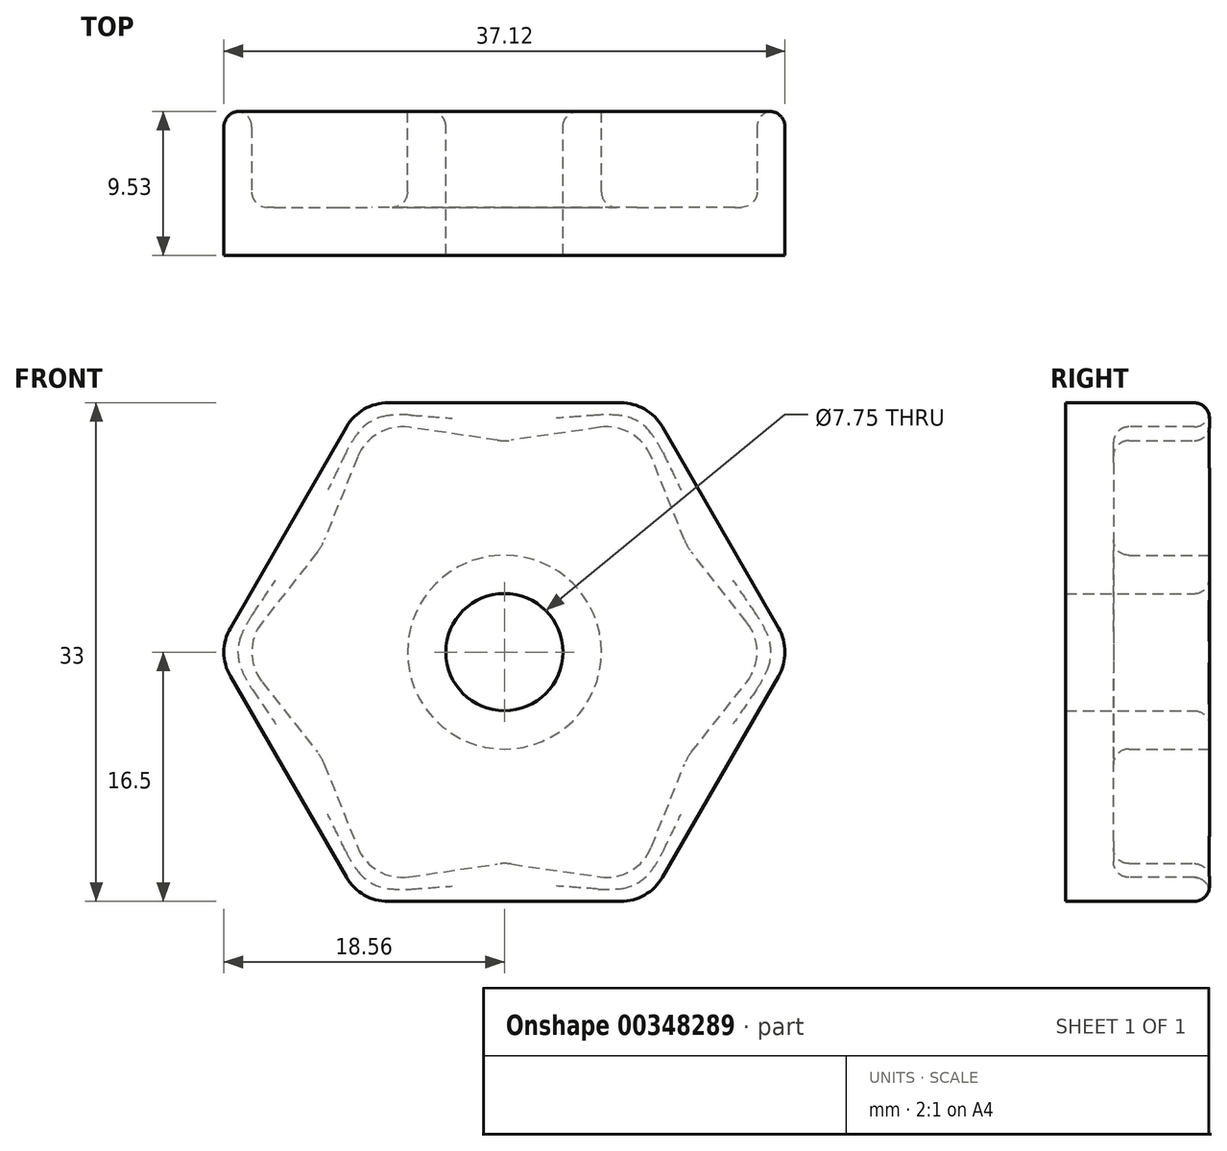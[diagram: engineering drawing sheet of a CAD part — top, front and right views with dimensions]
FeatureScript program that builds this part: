
annotation { "Feature Type Name" : "Feature", "Feature Type Description" : "" }
export const myFeature = defineFeature(function(context is Context, id is Id, definition is map)
    precondition{}
    {
        {
            var Q0;
            Q0=qCreatedBy(makeId("Front.planeOp"),FACE);
            var sketch = newSketch(context, id + "F0", { "sketchPlane" : qUnion([Q0])});
            skCircle(sketch, "E0.cCircle", {"center": v(0, 0) * mm, "radius": 16.5 * mm, "construction": true});
            skLineSegment(sketch, "E0.0", {"start": v(9.53, 16.5) * mm, "end": v(19.05, 0) * mm});
            skLineSegment(sketch, "E0.1", {"start": v(19.05, 0) * mm, "end": v(9.53, -16.5) * mm});
            skLineSegment(sketch, "E0.2", {"start": v(9.52, -16.5) * mm, "end": v(-9.53, -16.5) * mm});
            skLineSegment(sketch, "E0.3", {"start": v(-9.53, -16.5) * mm, "end": v(-19.05, 0) * mm});
            skLineSegment(sketch, "E0.4", {"start": v(-19.05, 0) * mm, "end": v(-9.52, 16.5) * mm});
            skLineSegment(sketch, "E0.5", {"start": v(-9.52, 16.5) * mm, "end": v(9.53, 16.5) * mm});
            skPoint(sketch, "E0.0.midPoint", {"position": v(14.29, 8.25) * mm});
            skLineSegment(sketch, "E1", {"start": v(0, 0) * mm, "end": v(-19.05, 0) * mm, "construction": true});
            skCircle(sketch, "E2", {"center": v(0, 0) * mm, "radius": 3.87 * mm});
            skSolve(sketch);
        }
        {
            var Q0;
            Q0 = qSketchRegion(id + "F0", true);
            extrude(context, id + "F1", {"entities" : qUnion([Q0]), "depth" : 9.52 * mm});
        }
        {
            var Q0;
            Q0=makeQuery(id+"F1.opExtrude","CAP_FACE",FACE,{"disambiguationData":[OSD([sQuery(id+"F0.wireOp",EDGE,"E0.0"),sQuery(id+"F0.wireOp",EDGE,"E0.1"),sQuery(id+"F0.wireOp",EDGE,"E0.2"),sQuery(id+"F0.wireOp",EDGE,"E0.3"),sQuery(id+"F0.wireOp",EDGE,"E0.4"),sQuery(id+"F0.wireOp",EDGE,"E0.5"),sQuery(id+"F0.wireOp",EDGE,"E2")])],"isStart":true});
            var sketch = newSketch(context, id + "F2", { "sketchPlane" : qUnion([Q0])});
            skLineSegment(sketch, "E3.0", {"start": v(-8.8, 15.23) * mm, "end": v(-17.58, 0) * mm, "construction": true});
            skLineSegment(sketch, "E3.1", {"start": v(-8.8, -15.23) * mm, "end": v(8.8, -15.23) * mm, "construction": true});
            skLineSegment(sketch, "E3.2", {"start": v(8.8, -15.23) * mm, "end": v(17.58, 0) * mm, "construction": true});
            skLineSegment(sketch, "E3.3", {"start": v(-17.58, 0) * mm, "end": v(-8.8, -15.23) * mm, "construction": true});
            skLineSegment(sketch, "E3.4", {"start": v(17.58, 0) * mm, "end": v(8.8, 15.23) * mm, "construction": true});
            skLineSegment(sketch, "E3.5", {"start": v(8.8, 15.23) * mm, "end": v(-8.8, 15.23) * mm, "construction": true});
            skCircle(sketch, "E4.0", {"center": v(0, 0) * mm, "radius": 6.41 * mm});
            skLineSegment(sketch, "E5", {"start": v(-17.58, 0) * mm, "end": v(-12.09, 6.98) * mm});
            skLineSegment(sketch, "E6", {"start": v(-12.09, 6.98) * mm, "end": v(-8.8, 15.23) * mm});
            skLineSegment(sketch, "E7", {"start": v(0, 0) * mm, "end": v(-13.19, 7.61) * mm, "construction": true});
            skLineSegment(sketch, "E8.1.0", {"start": v(-8.8, -15.23) * mm, "end": v(-12.09, -6.98) * mm});
            skLineSegment(sketch, "E8.1.1", {"start": v(-12.09, -6.98) * mm, "end": v(-17.58, 0) * mm});
            skLineSegment(sketch, "E8.2.0", {"start": v(8.8, -15.23) * mm, "end": v(0, -13.96) * mm});
            skLineSegment(sketch, "E8.2.1", {"start": v(0, -13.96) * mm, "end": v(-8.8, -15.23) * mm});
            skLineSegment(sketch, "E8.3.0", {"start": v(17.58, 0) * mm, "end": v(12.09, -6.98) * mm});
            skLineSegment(sketch, "E8.3.1", {"start": v(12.09, -6.98) * mm, "end": v(8.8, -15.23) * mm});
            skLineSegment(sketch, "E8.4.0", {"start": v(8.8, 15.23) * mm, "end": v(12.09, 6.98) * mm});
            skLineSegment(sketch, "E8.4.1", {"start": v(12.09, 6.98) * mm, "end": v(17.58, 0) * mm});
            skLineSegment(sketch, "E8.5.0", {"start": v(-8.8, 15.23) * mm, "end": v(0, 13.96) * mm});
            skLineSegment(sketch, "E8.5.1", {"start": v(0, 13.96) * mm, "end": v(8.8, 15.23) * mm});
            skSolve(sketch);
        }
        {
            var Q0;
            Q0 = qSketchRegion(id + "F2", true);
            extrude(context, id + "F3", {"entities" : qUnion([Q0]), "operationType" : NewBodyOperationType.REMOVE, "oppositeDirection" : true, "depth" : 6.35 * mm});
        }
        {
            var Q0;
            Q0=makeQuery(id+"F3.boolean.opBoolean","COPY",EDGE,{"derivedFrom":makeQuery(id+"F3.opExtrude","SWEPT_EDGE",EDGE,{"disambiguationData":[OSD([sQuery(id+"F2.wireOp",EDGE,"E8.3.0"),sQuery(id+"F2.wireOp",EDGE,"E8.4.1")])]})});
            var Q1;
            Q1=makeQuery(id+"F3.boolean.opBoolean","COPY",EDGE,{"derivedFrom":makeQuery(id+"F3.opExtrude","SWEPT_EDGE",EDGE,{"disambiguationData":[OSD([sQuery(id+"F2.wireOp",EDGE,"E8.4.0"),sQuery(id+"F2.wireOp",EDGE,"E8.4.1")])]})});
            var Q2;
            Q2=makeQuery(id+"F3.boolean.opBoolean","COPY",EDGE,{"derivedFrom":makeQuery(id+"F3.opExtrude","SWEPT_EDGE",EDGE,{"disambiguationData":[OSD([sQuery(id+"F2.wireOp",EDGE,"E8.4.0"),sQuery(id+"F2.wireOp",EDGE,"E8.5.1")])]})});
            var Q3;
            Q3=makeQuery(id+"F3.boolean.opBoolean","COPY",EDGE,{"derivedFrom":makeQuery(id+"F3.opExtrude","SWEPT_EDGE",EDGE,{"disambiguationData":[OSD([sQuery(id+"F2.wireOp",EDGE,"E8.5.0"),sQuery(id+"F2.wireOp",EDGE,"E8.5.1")])]})});
            var Q4;
            Q4=makeQuery(id+"F3.boolean.opBoolean","COPY",EDGE,{"derivedFrom":makeQuery(id+"F3.opExtrude","SWEPT_EDGE",EDGE,{"disambiguationData":[OSD([sQuery(id+"F2.wireOp",EDGE,"E6"),sQuery(id+"F2.wireOp",EDGE,"E8.5.0")])]})});
            var Q5;
            Q5=makeQuery(id+"F3.boolean.opBoolean","COPY",EDGE,{"derivedFrom":makeQuery(id+"F3.opExtrude","SWEPT_EDGE",EDGE,{"disambiguationData":[OSD([sQuery(id+"F2.wireOp",EDGE,"E5"),sQuery(id+"F2.wireOp",EDGE,"E6")])]})});
            var Q6;
            Q6=makeQuery(id+"F3.boolean.opBoolean","COPY",EDGE,{"derivedFrom":makeQuery(id+"F3.opExtrude","SWEPT_EDGE",EDGE,{"disambiguationData":[OSD([sQuery(id+"F2.wireOp",EDGE,"E5"),sQuery(id+"F2.wireOp",EDGE,"E8.1.1")])]})});
            var Q7;
            Q7=makeQuery(id+"F3.boolean.opBoolean","COPY",EDGE,{"derivedFrom":makeQuery(id+"F3.opExtrude","SWEPT_EDGE",EDGE,{"disambiguationData":[OSD([sQuery(id+"F2.wireOp",EDGE,"E8.1.0"),sQuery(id+"F2.wireOp",EDGE,"E8.1.1")])]})});
            var Q8;
            Q8=makeQuery(id+"F3.boolean.opBoolean","COPY",EDGE,{"derivedFrom":makeQuery(id+"F3.opExtrude","SWEPT_EDGE",EDGE,{"disambiguationData":[OSD([sQuery(id+"F2.wireOp",EDGE,"E8.1.0"),sQuery(id+"F2.wireOp",EDGE,"E8.2.1")])]})});
            var Q9;
            Q9=makeQuery(id+"F3.boolean.opBoolean","COPY",EDGE,{"derivedFrom":makeQuery(id+"F3.opExtrude","SWEPT_EDGE",EDGE,{"disambiguationData":[OSD([sQuery(id+"F2.wireOp",EDGE,"E8.2.0"),sQuery(id+"F2.wireOp",EDGE,"E8.2.1")])]})});
            var Q10;
            Q10=makeQuery(id+"F3.boolean.opBoolean","COPY",EDGE,{"derivedFrom":makeQuery(id+"F3.opExtrude","SWEPT_EDGE",EDGE,{"disambiguationData":[OSD([sQuery(id+"F2.wireOp",EDGE,"E8.2.0"),sQuery(id+"F2.wireOp",EDGE,"E8.3.1")])]})});
            var Q11;
            Q11=makeQuery(id+"F3.boolean.opBoolean","COPY",EDGE,{"derivedFrom":makeQuery(id+"F3.opExtrude","SWEPT_EDGE",EDGE,{"disambiguationData":[OSD([sQuery(id+"F2.wireOp",EDGE,"E8.3.0"),sQuery(id+"F2.wireOp",EDGE,"E8.3.1")])]})});
            var Q12;
            Q12=makeQuery(id+"F1.opExtrude","SWEPT_EDGE",EDGE,{"disambiguationData":[OSD([sQuery(id+"F0.wireOp",EDGE,"E0.4"),sQuery(id+"F0.wireOp",EDGE,"E0.5")])]});
            var Q13;
            Q13=makeQuery(id+"F1.opExtrude","SWEPT_EDGE",EDGE,{"disambiguationData":[OSD([sQuery(id+"F0.wireOp",EDGE,"E0.0"),sQuery(id+"F0.wireOp",EDGE,"E0.5")])]});
            var Q14;
            Q14=makeQuery(id+"F1.opExtrude","SWEPT_EDGE",EDGE,{"disambiguationData":[OSD([sQuery(id+"F0.wireOp",EDGE,"E0.0"),sQuery(id+"F0.wireOp",EDGE,"E0.1")])]});
            var Q15;
            Q15=makeQuery(id+"F1.opExtrude","SWEPT_EDGE",EDGE,{"disambiguationData":[OSD([sQuery(id+"F0.wireOp",EDGE,"E0.1"),sQuery(id+"F0.wireOp",EDGE,"E0.2")])]});
            var Q16;
            Q16=makeQuery(id+"F1.opExtrude","SWEPT_EDGE",EDGE,{"disambiguationData":[OSD([sQuery(id+"F0.wireOp",EDGE,"E0.3"),sQuery(id+"F0.wireOp",EDGE,"E0.4")])]});
            var Q17;
            Q17=makeQuery(id+"F1.opExtrude","SWEPT_EDGE",EDGE,{"disambiguationData":[OSD([sQuery(id+"F0.wireOp",EDGE,"E0.2"),sQuery(id+"F0.wireOp",EDGE,"E0.3")])]});
            fillet(context, id + "F4", {"entities" : qUnion([Q0, Q1, Q2, Q3, Q4, Q5, Q6, Q7, Q8, Q9, Q10, Q11, Q12, Q13, Q14, Q15, Q16, Q17]), "radius" : 3.18 * mm, "tangentPropagation" : true, "allowEdgeOverflow" : false});
        }
        {
            var Q0;
            Q0=makeQuery(id+"F3.boolean.opBoolean","COPY",FACE,{"derivedFrom":makeQuery(id+"F3.opExtrude","CAP_FACE",FACE,{"disambiguationData":[OSD([sQuery(id+"F2.wireOp",EDGE,"E4.0"),sQuery(id+"F2.wireOp",EDGE,"E5"),sQuery(id+"F2.wireOp",EDGE,"E6"),sQuery(id+"F2.wireOp",EDGE,"E8.1.0"),sQuery(id+"F2.wireOp",EDGE,"E8.1.1"),sQuery(id+"F2.wireOp",EDGE,"E8.2.0"),sQuery(id+"F2.wireOp",EDGE,"E8.2.1"),sQuery(id+"F2.wireOp",EDGE,"E8.3.0"),sQuery(id+"F2.wireOp",EDGE,"E8.3.1"),sQuery(id+"F2.wireOp",EDGE,"E8.4.0"),sQuery(id+"F2.wireOp",EDGE,"E8.4.1"),sQuery(id+"F2.wireOp",EDGE,"E8.5.0"),sQuery(id+"F2.wireOp",EDGE,"E8.5.1")])],"isStart":false})});
            var Q1;
            Q1=makeQuery(id+"F3.boolean.opBoolean","COPY",EDGE,{"derivedFrom":makeQuery(id+"F3.opExtrude","CAP_EDGE",EDGE,{"disambiguationData":[OSD([sQuery(id+"F2.wireOp",EDGE,"E4.0")])],"isStart":true})});
            var Q2;
            Q2=makeQuery(id+"F1.opExtrude","CAP_EDGE",EDGE,{"disambiguationData":[OSD([sQuery(id+"F0.wireOp",EDGE,"E2")])],"isStart":true});
            var Q3;
            {var subQ0=sQuery(id+"F2.wireOp",EDGE,"E8.1.1");var subQ1=sQuery(id+"F0.wireOp",EDGE,"E0.5");var subQ2=sQuery(id+"F2.wireOp",EDGE,"E5");var subQ3=sQuery(id+"F0.wireOp",EDGE,"E0.4");var subQ4=sQuery(id+"F0.wireOp",EDGE,"E0.0");var subQ5=sQuery(id+"F0.wireOp",EDGE,"E0.3");var subQ6=sQuery(id+"F0.wireOp",EDGE,"E0.1");var subQ7=sQuery(id+"F0.wireOp",EDGE,"E0.2");Q3=makeQuery(id+"F4.opFillet","BLEND_EDGE",EDGE,{"blendedFrom":[makeQuery(id+"F3.boolean.opBoolean","COPY",EDGE,{"derivedFrom":makeQuery(id+"F3.opExtrude","SWEPT_EDGE",EDGE,{"disambiguationData":[OSD([subQ2,subQ0])]})}),makeQuery(id+"F3.boolean.opBoolean","SPLIT",FACE,{"disambiguationData":[TD([makeQuery(id+"F1.opExtrude","SWEPT_FACE",FACE,{"disambiguationData":[OSD([subQ4])]})])],"derivedFrom":makeQuery(id+"F1.opExtrude","CAP_FACE",FACE,{"disambiguationData":[OSD([subQ4,subQ6,subQ7,subQ5,subQ3,subQ1,sQuery(id+"F0.wireOp",EDGE,"E2")])],"isStart":true})})],"blendedInto":[makeQuery(id+"F3.boolean.opBoolean","SPLIT",FACE,{"disambiguationData":[TD([makeQuery(id+"F1.opExtrude","SWEPT_FACE",FACE,{"disambiguationData":[OSD([subQ4])]})])],"derivedFrom":makeQuery(id+"F1.opExtrude","CAP_FACE",FACE,{"disambiguationData":[OSD([subQ4,subQ6,subQ7,subQ5,subQ3,subQ1,sQuery(id+"F0.wireOp",EDGE,"E2")])],"isStart":true})})]});}
            var Q4;
            {var subQ0=sQuery(id+"F0.wireOp",EDGE,"E0.5");var subQ1=sQuery(id+"F0.wireOp",EDGE,"E0.4");var subQ2=sQuery(id+"F0.wireOp",EDGE,"E0.0");var subQ3=sQuery(id+"F0.wireOp",EDGE,"E0.3");var subQ4=sQuery(id+"F0.wireOp",EDGE,"E0.1");var subQ5=sQuery(id+"F0.wireOp",EDGE,"E0.2");Q4=makeQuery(id+"F4.opFillet","BLEND_EDGE",EDGE,{"blendedFrom":[makeQuery(id+"F1.opExtrude","SWEPT_EDGE",EDGE,{"disambiguationData":[OSD([subQ2,subQ4])]}),makeQuery(id+"F3.boolean.opBoolean","SPLIT",FACE,{"disambiguationData":[TD([makeQuery(id+"F1.opExtrude","SWEPT_FACE",FACE,{"disambiguationData":[OSD([subQ2])]})])],"derivedFrom":makeQuery(id+"F1.opExtrude","CAP_FACE",FACE,{"disambiguationData":[OSD([subQ2,subQ4,subQ5,subQ3,subQ1,subQ0,sQuery(id+"F0.wireOp",EDGE,"E2")])],"isStart":true})})],"blendedInto":[makeQuery(id+"F3.boolean.opBoolean","SPLIT",FACE,{"disambiguationData":[TD([makeQuery(id+"F1.opExtrude","SWEPT_FACE",FACE,{"disambiguationData":[OSD([subQ2])]})])],"derivedFrom":makeQuery(id+"F1.opExtrude","CAP_FACE",FACE,{"disambiguationData":[OSD([subQ2,subQ4,subQ5,subQ3,subQ1,subQ0,sQuery(id+"F0.wireOp",EDGE,"E2")])],"isStart":true})})]});}
            fillet(context, id + "F5", {"entities" : qUnion([Q0, Q1, Q2, Q3, Q4]), "radius" : 1.02 * mm, "tangentPropagation" : true, "allowEdgeOverflow" : false});
        }
    });
